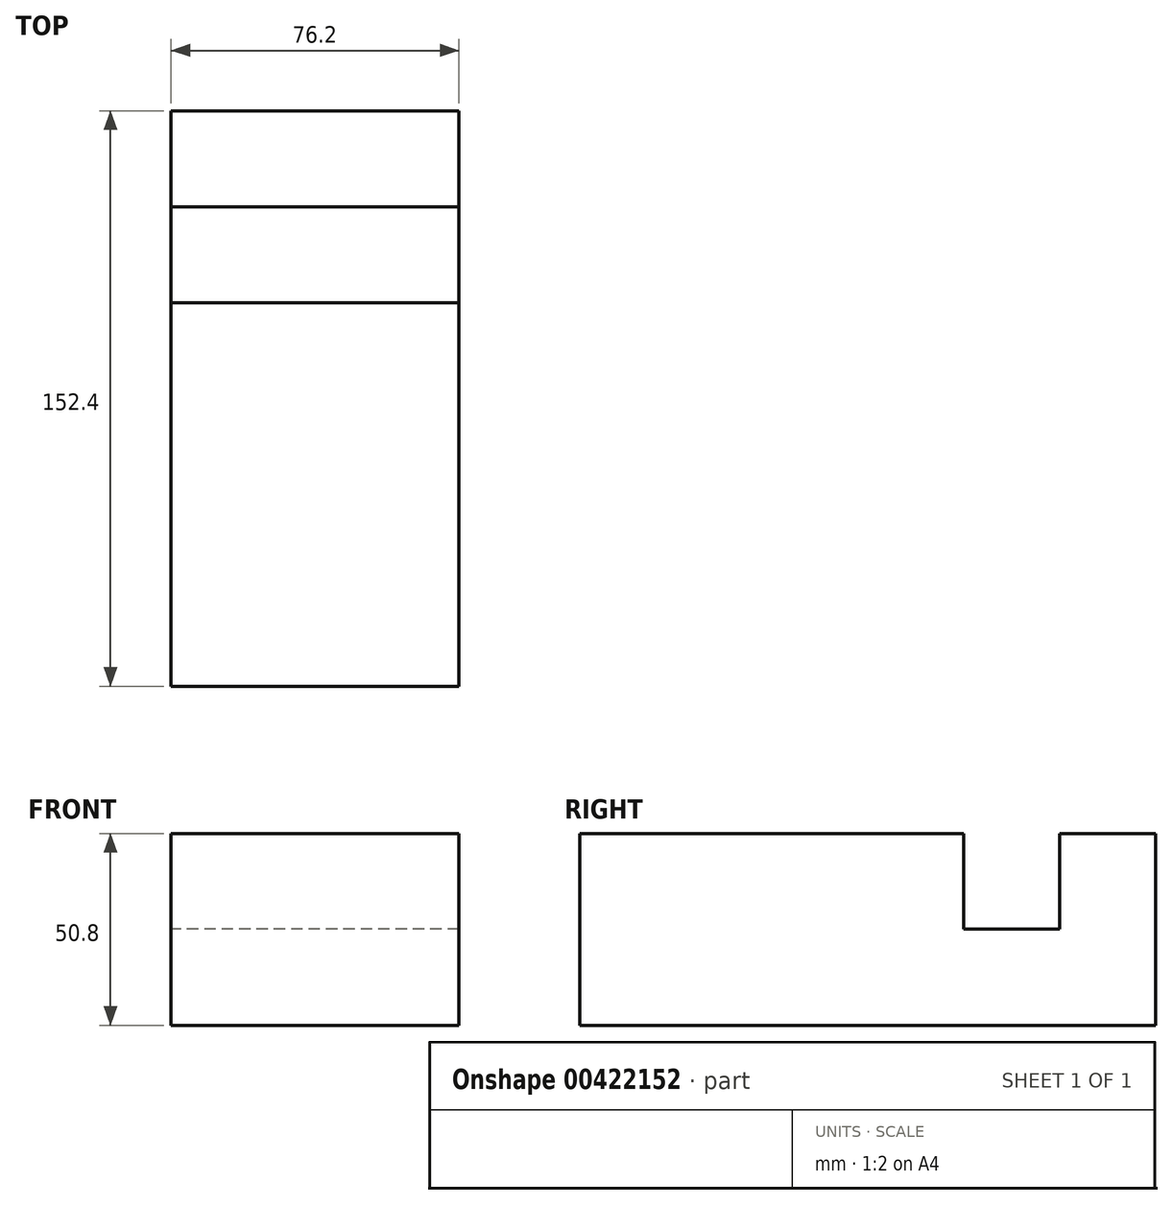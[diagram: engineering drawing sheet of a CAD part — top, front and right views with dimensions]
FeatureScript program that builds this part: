
annotation { "Feature Type Name" : "Feature", "Feature Type Description" : "" }
export const myFeature = defineFeature(function(context is Context, id is Id, definition is map)
    precondition{}
    {
        {
            var Q0;
            Q0=qCreatedBy(makeId("Front.planeOp"),FACE);
            var sketch = newSketch(context, id + "F0", { "sketchPlane" : qUnion([Q0])});
            skLineSegment(sketch, "E0", {"start": v(0, 0) * mm, "end": v(76.2, 0) * mm});
            skLineSegment(sketch, "E1", {"start": v(76.2, 0) * mm, "end": v(76.2, 50.8) * mm});
            skLineSegment(sketch, "E2", {"start": v(76.2, 50.8) * mm, "end": v(0, 50.8) * mm});
            skLineSegment(sketch, "E3", {"start": v(0, 50.8) * mm, "end": v(0, 0) * mm});
            skSolve(sketch);
        }
        {
            var Q0;
            Q0=makeQuery(id+"F0.imprint","IMPRINT",FACE,{"disambiguationData":[TD([[makeQuery(id+"F0.imprint","IMPRINT",EDGE,{"derivedFrom":sQuery(id+"F0.wireOp",EDGE,"E0")}),1.0]])]});
            extrude(context, id + "F1", {"entities" : qUnion([Q0]), "depth" : 152.4 * mm});
        }
        {
            var Q0;
            Q0=makeQuery(id+"F1.opExtrude","SWEPT_FACE",FACE,{"disambiguationData":[OSD([sQuery(id+"F0.wireOp",EDGE,"E3")])]});
            var sketch = newSketch(context, id + "F2", { "sketchPlane" : qUnion([Q0])});
            skSolve(sketch);
        }
        {
            var Q0;
            {var subQ0=sQuery(id+"F0.wireOp",EDGE,"E3");Q0=makeQuery(id+"F2.imprint","IMPRINT",FACE,{"disambiguationData":[TD([[makeQuery(id+"F2.imprint","IMPRINT",EDGE,{"derivedFrom":makeQuery(id+"F1.opExtrude","CAP_EDGE",EDGE,{"disambiguationData":[OSD([subQ0])],"isStart":true})}),1.0]])]});}
            var sketch = newSketch(context, id + "F3", { "sketchPlane" : qUnion([Q0])});
            skLineSegment(sketch, "E4", {"start": v(25.4, 50.9) * mm, "end": v(25.4, 25.5) * mm});
            skLineSegment(sketch, "E5", {"start": v(25.4, 25.5) * mm, "end": v(50.8, 25.5) * mm});
            skLineSegment(sketch, "E6", {"start": v(50.8, 25.5) * mm, "end": v(50.8, 50.9) * mm});
            skSolve(sketch);
        }
        {
            var Q0;
            {var subQ0=sQuery(id+"F3.wireOp",EDGE,"E5");Q0=makeQuery(id+"F3.imprint","IMPRINT",FACE,{"disambiguationData":[TD([[makeQuery(id+"F3.imprint","IMPRINT",EDGE,{"derivedFrom":subQ0}),1.0]])]});}
            extrude(context, id + "F4", {"entities" : qUnion([Q0]), "operationType" : NewBodyOperationType.REMOVE, "oppositeDirection" : true, "depth" : 76.2 * mm});
        }
    });
